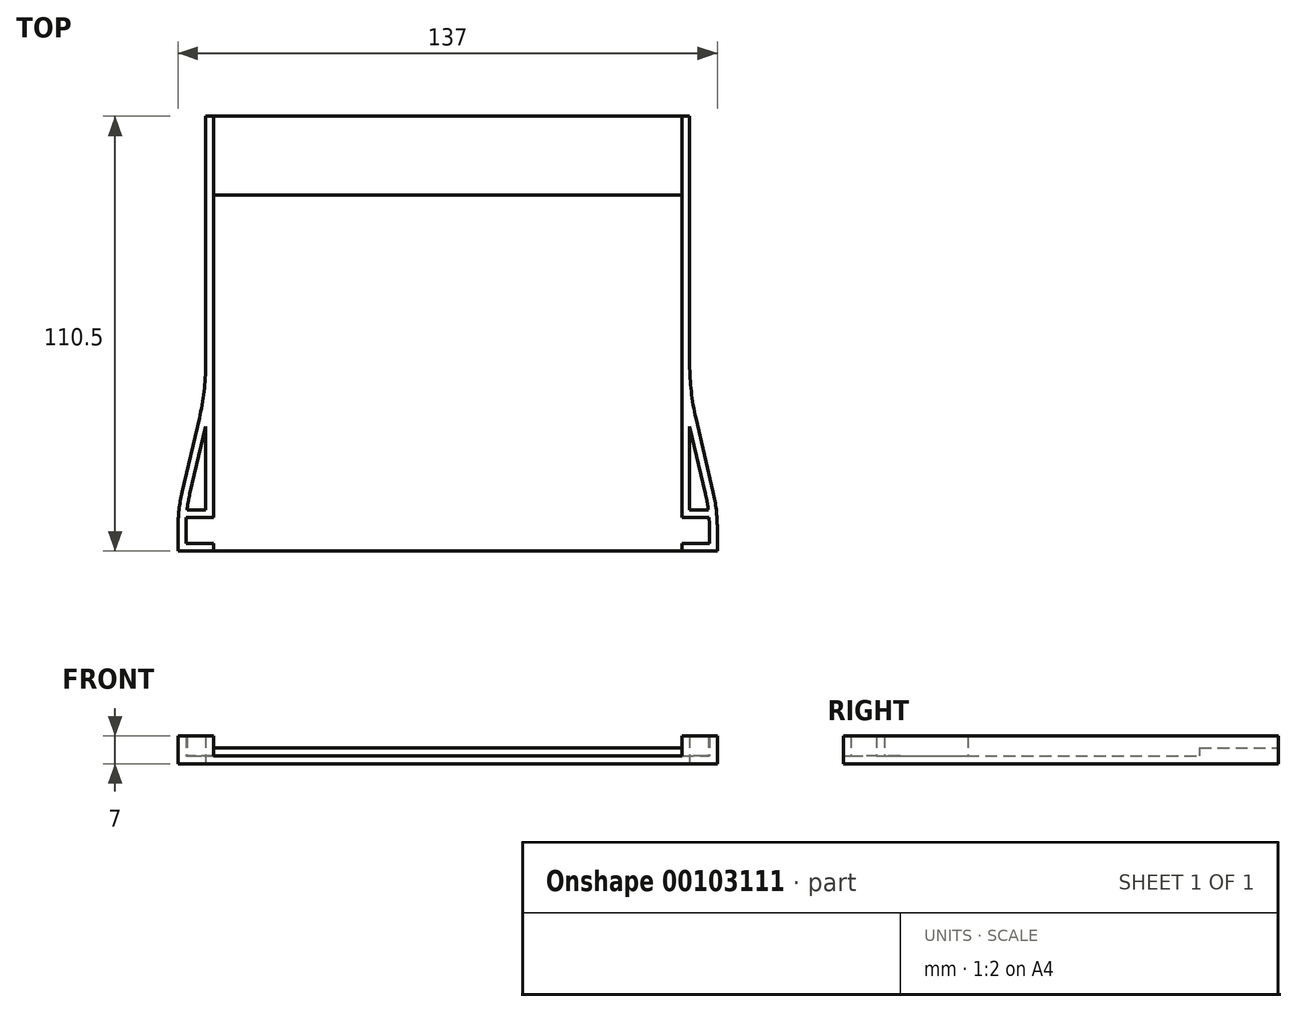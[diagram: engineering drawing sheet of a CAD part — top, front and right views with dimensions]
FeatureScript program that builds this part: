
annotation { "Feature Type Name" : "Feature", "Feature Type Description" : "" }
export const myFeature = defineFeature(function(context is Context, id is Id, definition is map)
    precondition{}
    {
        {
            var Q0;
            Q0=qCreatedBy(makeId("Top.planeOp"),FACE);
            var sketch = newSketch(context, id + "F0", { "sketchPlane" : qUnion([Q0])});
            skLineSegment(sketch, "E0.bottom", {"start": v(0, 0) * mm, "end": v(68.5, 0) * mm});
            skLineSegment(sketch, "E0.left", {"start": v(0, 0) * mm, "end": v(0, 10.5) * mm});
            skLineSegment(sketch, "E1.top", {"start": v(68.5, 110.5) * mm, "end": v(7, 110.5) * mm});
            skLineSegment(sketch, "E1.right", {"start": v(7, 40.5) * mm, "end": v(7, 110.5) * mm});
            skLineSegment(sketch, "E2", {"start": v(0, 10.5) * mm, "end": v(7, 40.5) * mm});
            skLineSegment(sketch, "E3", {"start": v(68.5, 110.5) * mm, "end": v(68.5, 0) * mm, "construction": true});
            skLineSegment(sketch, "E4.MirrorCS", {"start": v(68.5, 110.5) * mm, "end": v(130, 110.5) * mm});
            skLineSegment(sketch, "E5.MirrorCS", {"start": v(130, 40.5) * mm, "end": v(130, 110.5) * mm});
            skLineSegment(sketch, "E6.MirrorCS", {"start": v(137, 10.5) * mm, "end": v(130, 40.5) * mm});
            skLineSegment(sketch, "E7.MirrorCS", {"start": v(137, 0) * mm, "end": v(137, 10.5) * mm});
            skLineSegment(sketch, "E8.MirrorCS", {"start": v(137, 0) * mm, "end": v(68.5, 0) * mm});
            skSolve(sketch);
        }
        {
            var Q0;
            Q0=makeQuery(id+"F0.imprint","IMPRINT",FACE,{"disambiguationData":[TD([[makeQuery(id+"F0.imprint","IMPRINT",EDGE,{"derivedFrom":sQuery(id+"F0.wireOp",EDGE,"E0.bottom")}),1.0]])]});
            extrude(context, id + "F1", {"entities" : qUnion([Q0]), "depth" : 2 * mm});
        }
        {
            var Q0;
            Q0=makeQuery(id+"F1.opExtrude","SWEPT_EDGE",EDGE,{"disambiguationData":[OSD([sQuery(id+"F0.wireOp",EDGE,"E6.MirrorCS"),sQuery(id+"F0.wireOp",EDGE,"E7.MirrorCS")])]});
            var Q1;
            Q1=makeQuery(id+"F1.opExtrude","SWEPT_EDGE",EDGE,{"disambiguationData":[OSD([sQuery(id+"F0.wireOp",EDGE,"E0.left"),sQuery(id+"F0.wireOp",EDGE,"E2")])]});
            fillet(context, id + "F2", {"entities" : qUnion([Q0, Q1]), "radius" : 40 * mm, "tangentPropagation" : true, "allowEdgeOverflow" : false});
        }
        {
            var Q0;
            Q0=makeQuery(id+"F1.opExtrude","SWEPT_EDGE",EDGE,{"disambiguationData":[OSD([sQuery(id+"F0.wireOp",EDGE,"E1.right"),sQuery(id+"F0.wireOp",EDGE,"E2")])]});
            var Q1;
            Q1=makeQuery(id+"F1.opExtrude","SWEPT_EDGE",EDGE,{"disambiguationData":[OSD([sQuery(id+"F0.wireOp",EDGE,"E5.MirrorCS"),sQuery(id+"F0.wireOp",EDGE,"E6.MirrorCS")])]});
            fillet(context, id + "F3", {"entities" : qUnion([Q0, Q1]), "radius" : 60 * mm, "tangentPropagation" : true, "allowEdgeOverflow" : false});
        }
        {
            var Q0;
            Q0=makeQuery(id+"F1.opExtrude","CAP_FACE",FACE,{"disambiguationData":[OSD([sQuery(id+"F0.wireOp",EDGE,"E0.bottom"),sQuery(id+"F0.wireOp",EDGE,"E0.left"),sQuery(id+"F0.wireOp",EDGE,"E1.top"),sQuery(id+"F0.wireOp",EDGE,"E1.right"),sQuery(id+"F0.wireOp",EDGE,"E2"),sQuery(id+"F0.wireOp",EDGE,"E4.MirrorCS"),sQuery(id+"F0.wireOp",EDGE,"E5.MirrorCS"),sQuery(id+"F0.wireOp",EDGE,"E6.MirrorCS"),sQuery(id+"F0.wireOp",EDGE,"E7.MirrorCS"),sQuery(id+"F0.wireOp",EDGE,"E8.MirrorCS")])],"isStart":false});
            var sketch = newSketch(context, id + "F4", { "sketchPlane" : qUnion([Q0])});
            skLineSegment(sketch, "E9.0", {"start": v(9, 47.4) * mm, "end": v(9, 110.5) * mm});
            skLineSegment(sketch, "E9.6", {"start": v(2, 2) * mm, "end": v(9, 2) * mm});
            skLineSegment(sketch, "E9.7", {"start": v(2, 2) * mm, "end": v(2, 5.9) * mm});
            skArc(sketch, "E9.8", {"start": v(3, 14.53) * mm, "mid": v(2.58, 12.52) * mm, "end": v(2.28, 10.5) * mm});
            skLineSegment(sketch, "E9.9", {"start": v(3, 14.53) * mm, "end": v(7, 31.7) * mm});
            skLineSegment(sketch, "E9.10", {"start": v(9, 47.4) * mm, "end": v(9, 47.4) * mm});
            skLineSegment(sketch, "E10.right", {"start": v(9, 0) * mm, "end": v(9, 2) * mm});
            skLineSegment(sketch, "E11.MirrorCS", {"start": v(128, 0) * mm, "end": v(128, 2) * mm});
            skLineSegment(sketch, "E12.trimOffspring", {"start": v(128, 2) * mm, "end": v(135, 2) * mm});
            skPoint(sketch, "E10.left.start.orphan", {"position": v(68.5, 0) * mm});
            skLineSegment(sketch, "E13", {"start": v(9, 8.5) * mm, "end": v(2.09, 8.5) * mm});
            skLineSegment(sketch, "E14", {"start": v(9, 8.5) * mm, "end": v(9, 47.4) * mm});
            skLineSegment(sketch, "E15", {"start": v(2.28, 10.5) * mm, "end": v(7, 10.5) * mm});
            skLineSegment(sketch, "E16", {"start": v(7, 10.5) * mm, "end": v(7, 31.7) * mm});
            skArc(sketch, "E17.trimOffspring", {"start": v(2.09, 8.5) * mm, "mid": v(2.02, 7.2) * mm, "end": v(2, 5.9) * mm});
            skLineSegment(sketch, "E18", {"start": v(68.5, 0) * mm, "end": v(68.5, 110.5) * mm, "construction": true});
            skLineSegment(sketch, "E19.MirrorCS", {"start": v(128, 47.4) * mm, "end": v(128, 47.4) * mm});
            skPoint(sketch, "E20.MirrorCS.end.orphan", {"position": v(128, 47.4) * mm});
            skLineSegment(sketch, "E21.MirrorCS", {"start": v(135, 2) * mm, "end": v(135, 5.9) * mm});
            skArc(sketch, "E22.MirrorCS", {"start": v(134.91, 8.5) * mm, "mid": v(134.98, 7.2) * mm, "end": v(135, 5.9) * mm});
            skLineSegment(sketch, "E23.MirrorCS", {"start": v(128, 8.5) * mm, "end": v(134.91, 8.5) * mm});
            skLineSegment(sketch, "E24.MirrorCS", {"start": v(128, 8.5) * mm, "end": v(128, 47.4) * mm});
            skLineSegment(sketch, "E25.MirrorCS", {"start": v(130, 10.5) * mm, "end": v(130, 31.7) * mm});
            skLineSegment(sketch, "E26.MirrorCS", {"start": v(134.72, 10.5) * mm, "end": v(130, 10.5) * mm});
            skArc(sketch, "E27.MirrorCS", {"start": v(134, 14.53) * mm, "mid": v(134.42, 12.52) * mm, "end": v(134.72, 10.5) * mm});
            skLineSegment(sketch, "E28.MirrorCS", {"start": v(134, 14.53) * mm, "end": v(130, 31.7) * mm});
            skLineSegment(sketch, "E29.MirrorCS", {"start": v(128, 47.4) * mm, "end": v(128, 110.5) * mm});
            skSolve(sketch);
        }
        {
            var Q0;
            {var subQ0=sQuery(id+"F4.wireOp",EDGE,"E11.MirrorCS");Q0=makeQuery(id+"F4.imprint","IMPRINT",FACE,{"disambiguationData":[TD([[makeQuery(id+"F4.imprint","IMPRINT",EDGE,{"derivedFrom":subQ0}),-1.0]])]});}
            var Q1;
            {var subQ6=sQuery(id+"F4.wireOp",EDGE,"E9.0");Q1=makeQuery(id+"F4.imprint","IMPRINT",FACE,{"disambiguationData":[TD([[makeQuery(id+"F4.imprint","IMPRINT",EDGE,{"derivedFrom":subQ6}),1.0]])]});}
            extrude(context, id + "F5", {"entities" : qUnion([Q0, Q1]), "operationType" : NewBodyOperationType.ADD, "depth" : 5 * mm});
        }
        {
            var Q0;
            {var subQ0=sQuery(id+"F0.wireOp",EDGE,"E5.MirrorCS");var subQ1=sQuery(id+"F0.wireOp",EDGE,"E4.MirrorCS");var subQ2=sQuery(id+"F0.wireOp",EDGE,"E1.top");var subQ5=sQuery(id+"F0.wireOp",EDGE,"E8.MirrorCS");var subQ6=sQuery(id+"F0.wireOp",EDGE,"E0.bottom");var subQ7=sQuery(id+"F0.wireOp",EDGE,"E0.left");var subQ12=sQuery(id+"F0.wireOp",EDGE,"E7.MirrorCS");var subQ13=sQuery(id+"F0.wireOp",EDGE,"E1.right");Q0=makeQuery(id+"F5.boolean.opBoolean","SPLIT",FACE,{"disambiguationData":[TD([makeQuery(id+"F5.opExtrude","SWEPT_FACE",FACE,{"disambiguationData":[OSD([sQuery(id+"F4.wireOp",EDGE,"E9.6")])]})])],"derivedFrom":makeQuery(id+"F1.opExtrude","CAP_FACE",FACE,{"disambiguationData":[OSD([subQ6,subQ7,subQ2,subQ13,sQuery(id+"F0.wireOp",EDGE,"E2"),subQ1,subQ0,sQuery(id+"F0.wireOp",EDGE,"E6.MirrorCS"),subQ12,subQ5])],"isStart":false})});}
            var sketch = newSketch(context, id + "F6", { "sketchPlane" : qUnion([Q0])});
            skLineSegment(sketch, "E30.bottom", {"start": v(9, 110.5) * mm, "end": v(128, 110.5) * mm});
            skLineSegment(sketch, "E30.top", {"start": v(9, 90.5) * mm, "end": v(128, 90.5) * mm});
            skLineSegment(sketch, "E30.left", {"start": v(9, 110.5) * mm, "end": v(9, 90.5) * mm});
            skLineSegment(sketch, "E30.right", {"start": v(128, 110.5) * mm, "end": v(128, 90.5) * mm});
            skSolve(sketch);
        }
        {
            var Q0;
            Q0 = qSketchRegion(id + "F6", true);
            extrude(context, id + "F7", {"entities" : qUnion([Q0]), "operationType" : NewBodyOperationType.ADD, "depth" : 2 * mm});
        }
    });
